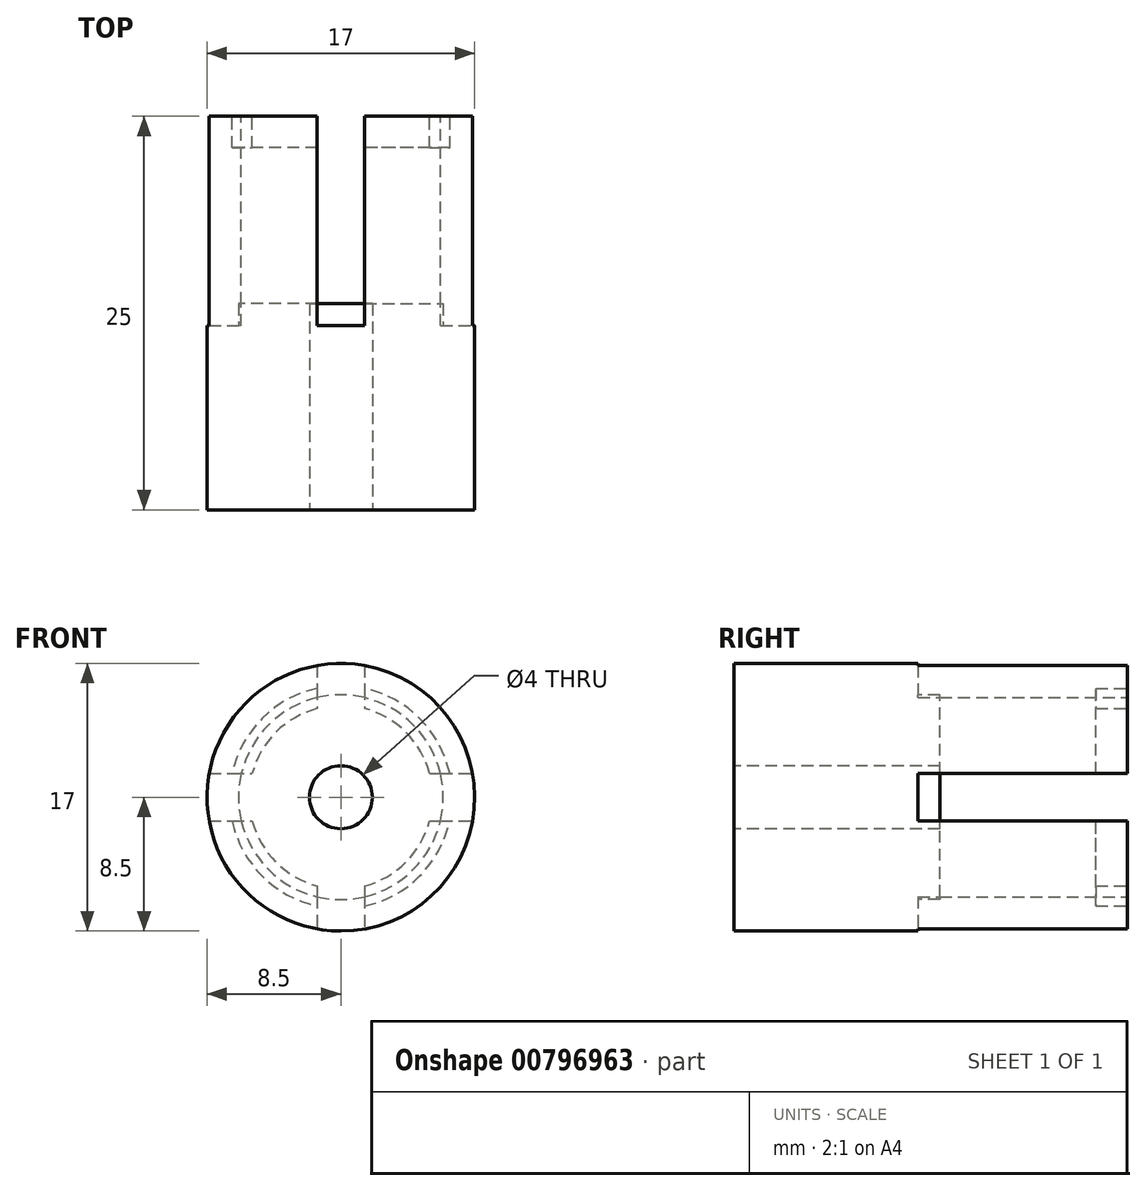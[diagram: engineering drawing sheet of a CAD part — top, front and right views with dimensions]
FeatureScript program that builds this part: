
annotation { "Feature Type Name" : "Feature", "Feature Type Description" : "" }
export const myFeature = defineFeature(function(context is Context, id is Id, definition is map)
    precondition{}
    {
        {
            var Q0;
            Q0=qCreatedBy(makeId("Front.planeOp"),FACE);
            var sketch = newSketch(context, id + "F0", { "sketchPlane" : qUnion([Q0])});
            skCircle(sketch, "E0", {"center": v(0, 0) * mm, "radius": 6.5 * mm});
            skCircle(sketch, "E1", {"center": v(0, 0) * mm, "radius": 8.5 * mm});
            skSolve(sketch);
        }
        {
            var Q0;
            Q0=makeQuery(id+"F0.imprint","IMPRINT",FACE,{"disambiguationData":[TD([[makeQuery(id+"F0.imprint","IMPRINT",EDGE,{"derivedFrom":sQuery(id+"F0.wireOp",EDGE,"E0")}),-1.0]])]});
            extrude(context, id + "F1", {"entities" : qUnion([Q0]), "depth" : 25 * mm, "offsetDistance" : 25 * mm});
        }
        {
            var Q0;
            {var subQ0=sQuery(id+"F0.wireOp",EDGE,"E0");var subQ1=sQuery(id+"F0.wireOp",EDGE,"E1");var subQ2=sQuery(id+"F4.wireOp",EDGE,"E4.top");Q0=makeQuery(id+"Frz9UKNco3ceUcC_1.boolean.opBoolean","SPLIT",FACE,{"disambiguationData":[TD([makeQuery(id+"Frz9UKNco3ceUcC_1.opExtrude","SWEPT_FACE",FACE,{"disambiguationData":[OSD([subQ2]),TDD([makeQuery(id+"F4.imprint","IMPRINT",EDGE,{"disambiguationData":[TD([[makeQuery(id+"F4.imprint","INTERSECT",VERTEX,{"derivedFrom":[subQ2,sQuery(id+"F4.wireOp",EDGE,"E4.left")]}),-1.0]])],"derivedFrom":subQ2})])]})])],"derivedFrom":makeQuery(id+"F1.opExtrude","CAP_FACE",FACE,{"disambiguationData":[OSD([subQ0,subQ1])],"isStart":true})});}
            var sketch = newSketch(context, id + "F2", { "sketchPlane" : qUnion([Q0])});
            skCircle(sketch, "E2", {"center": v(0, 0) * mm, "radius": 5.84 * mm});
            skCircle(sketch, "E3.0", {"center": v(0, 0) * mm, "radius": 7.08 * mm});
            skSolve(sketch);
        }
        {
            var Q0;
            Q0 = qSketchRegion(id + "F2", true);
            extrude(context, id + "F3", {"entities" : qUnion([Q0]), "oppositeDirection" : true, "depth" : 2 * mm, "offsetDistance" : 25 * mm});
        }
        {
            var Q0;
            Q0=qCreatedBy(makeId("Front.planeOp"),FACE);
            var sketch = newSketch(context, id + "F4", { "sketchPlane" : qUnion([Q0])});
            skLineSegment(sketch, "E4.bottom", {"start": v(-12.27, 1.5) * mm, "end": v(12.27, 1.5) * mm});
            skLineSegment(sketch, "E4.top", {"start": v(-12.27, -1.5) * mm, "end": v(12.27, -1.5) * mm});
            skLineSegment(sketch, "E4.left", {"start": v(-12.27, 1.5) * mm, "end": v(-12.27, -1.5) * mm});
            skLineSegment(sketch, "E4.right", {"start": v(12.27, 1.5) * mm, "end": v(12.27, -1.5) * mm});
            skPoint(sketch, "E4.middle", {"position": v(0, 0) * mm});
            skLineSegment(sketch, "E5.bottom", {"start": v(-1.5, 11.96) * mm, "end": v(1.5, 11.96) * mm});
            skLineSegment(sketch, "E5.top", {"start": v(-1.5, -11.96) * mm, "end": v(1.5, -11.96) * mm});
            skLineSegment(sketch, "E5.left", {"start": v(-1.5, 11.96) * mm, "end": v(-1.5, -11.96) * mm});
            skLineSegment(sketch, "E5.right", {"start": v(1.5, 11.96) * mm, "end": v(1.5, -11.96) * mm});
            skSolve(sketch);
        }
        {
            var Q0;
            Q0 = qSketchRegion(id + "F4", true);
            extrude(context, id + "F5", {"entities" : qUnion([Q0]), "operationType" : NewBodyOperationType.REMOVE, "depth" : 13.3 * mm, "offsetDistance" : 25 * mm});
        }
        {
            var Q0;
            Q0=makeQuery(id+"F1.opExtrude","CAP_FACE",FACE,{"disambiguationData":[OSD([sQuery(id+"F0.wireOp",EDGE,"E0"),sQuery(id+"F0.wireOp",EDGE,"E1")])],"isStart":false});
            var sketch = newSketch(context, id + "F6", { "sketchPlane" : qUnion([Q0])});
            skCircle(sketch, "E6", {"center": v(0, 0) * mm, "radius": 2 * mm});
            skCircle(sketch, "E7.0", {"center": v(0, 0) * mm, "radius": 7 * mm});
            skSolve(sketch);
        }
        {
            var Q0;
            Q0=makeQuery(id+"F6.imprint","IMPRINT",FACE,{"disambiguationData":[TD([[makeQuery(id+"F6.imprint","IMPRINT",EDGE,{"derivedFrom":sQuery(id+"F6.wireOp",EDGE,"E6")}),-1.0]])]});
            extrude(context, id + "F7", {"entities" : qUnion([Q0]), "operationType" : NewBodyOperationType.ADD, "oppositeDirection" : true, "depth" : 13.1 * mm, "offsetDistance" : 25 * mm});
        }
    });
